# Revit family: Shower-Bath_and_Shower_Trim-KOHLER-Bancroft-K-TS10582_1
name_source: partatom
category: Plumbing Fixtures
revit_build: Autodesk Revit 2017 (Build: 20160225_1515(x64)
units: mm (PartAtom-declared; Revit-internal decimal feet)

## family parameters
Cut with Voids When Loaded = No
Host = Face
OmniClass Number = 23.31.17.00
OmniClass Title = Showers
Part Type = Normal
Room Calculation Point = No
Round Connector Dimension = Use Diameter
Shared = No

## types (4) — shared parameters
ADA Compliant = No
Assembly Code = D2010700
CW Connection = No
Cold Water Inlet = Cold Water Inlet
Date Modified = 01/29/2020
Default Elevation = 42"
Description = Rite-Temp® bath and shower valve trim with metal lever handle, slip-fit spout and 2.5 gpm showerhead
Drain Included = No
Flow Rate = 3 GPM
HW Connection = Yes
Handle Clearance = 3 3/16"
Height = 6 3/8"
Hot Water Inlet = Tempered Water Inlet 1
Length = 6 7/8"
Manufacturer = KOHLER Co.
MasterFormat 1995 = 15410
MasterFormat 2004 = 22.41.23
Material = Premium Metal Construction
Pressure = 80.00 psi
Product Documentation Link = https://www.us.kohler.com
Product Name = Bancroft
Product Page URL = http://www.us.kohler.com
Tempered Water Inlet 2 = Tempered Water Inlet 2
URL = https://www.us.kohler.com
Vent Connection = No
Waste Connection = No
Waste Water Outlet = Waste Water Outlet
WaterSense Certified = No
Width = 6 3/8"

## per-type parameters (varying)
| type | Finish | Model | Type |
| CP-Polished Chrome | Kohler-Metal-CP-Polished_Chrome | K-TS10582-4-CP | 1 |
| SN-Vibrant Polished Nickel | Kohler-Metal-SN-Vibrant_Polished_Nickel | K-TS10582-4-SN | 2 |
| BN-Vibrant Brushed Nickel | Kohler-Metal-BN-Vibrant_Brushed_Nickel | K-TS10582-4-BN | 3 |
| 2BZ-Oil-Rubbed Bronze | Kohler-Metal-2BZ-Oil_Rubbed_Bronze | K-TS10582-4-2BZ | 4 |

## geometry (parser evidence)
native form markers: Sweep x7
no freeform markers — native parametric forms only
